# Revit family: Holocom-SDS Connector-2015
name_source: partatom
category: Security Devices
revit_build: Autodesk Revit 2015 (Build: 20140606_1530(x64)
units: mm (PartAtom-declared; Revit-internal decimal feet)

## types (14) — shared parameters
Default Elevation = 4' - 0"
Manufacturer = Holocom
Offset = 0' - 1"
Product Page URL = http://www.holocom.com
URL = www.holocom.com

## per-type parameters (varying)
| type | 3-way | 3-way Internal | 3-way Reducing | 3-way Run End | 45 Deg External | 45 Deg Internal | 90 Deg | 90 Deg Internal | Interface Sleeve | Interface Sleeve 90 | Material | Model | Offset 4" | Offset 8" | Product Notes | Run End | Universal Connector |
| SDS_90 Deg Connector | No | No | No | No | No | No | Yes | No | No | No | <By Category> | SDS-CT-090 | No | No |  | No | No |
| SDS_3-way Reducing Connector | No | No | Yes | No | No | No | No | No | No | No | <By Category> | SMD-CT-3WY | No | No | Connectection to MiniDukt | No | No |
| SDS_3-way Connector | Yes | No | No | No | No | No | No | No | No | No | <By Category> | SDS-CT-3WY | No | No |  | No | No |
| SDS_3-way Internal Connector | No | Yes | No | No | No | No | No | No | No | No | <By Category> | SDS-CT-3IN | No | No |  | No | No |
| SDS_3-way Run End Connector | No | No | No | Yes | No | No | No | No | No | No | <By Category> | SMD-3WY-REC-LT-RT | No | No | Connection to MiniDukt | No | No |
| SDS_90 Deg Internal Connector | No | No | No | No | No | No | No | Yes | No | No | <By Category> | SDS-CT-90i | No | No |  | No | No |
| SDS_45 Deg External Connector | No | No | No | No | Yes | No | No | No | No | No | <By Category> | SDS-CT-45e | No | No |  | No | No |
| SDS_45 Deg Internal Connector | No | No | No | No | No | Yes | No | No | No | No | <By Category> | SDS-CT-45i | No | No |  | No | No |
| SDS_Interface Sleeve 90 | No | No | No | No | No | No | No | No | No | Yes | <By Category> | SDS-CT-INF-90 | No | No |  | No | No |
| SDS_Offset 4" Connector | No | No | No | No | No | No | No | No | No | No | <By Category> | SDS-CT-OFF-04 | Yes | No |  | No | No |
| SDS_Offset 8" Connector | No | No | No | No | No | No | No | No | No | No | <By Category> | SDS-CT-OFF-08 | No | Yes |  | No | No |
| SDS_Run End Connector | No | No | No | No | No | No | No | No | No | No | <By Category> | SDS-WM-REC | No | No |  | Yes | No |
| SDS_Interface Sleeve | No | No | No | No | No | No | No | No | Yes | No | <By Category> | SDS-CT-INF-ST | No | No |  | No | No |
| SDS_Universal Connector | No | No | No | No | No | No | No | No | No | No | Holocom_WhiteTextured | SDS-CT-UNI | No | No |  | No | Yes |

## geometry (parser evidence)
native form markers: Extrusion x2, Sweep x35
no freeform markers — native parametric forms only
